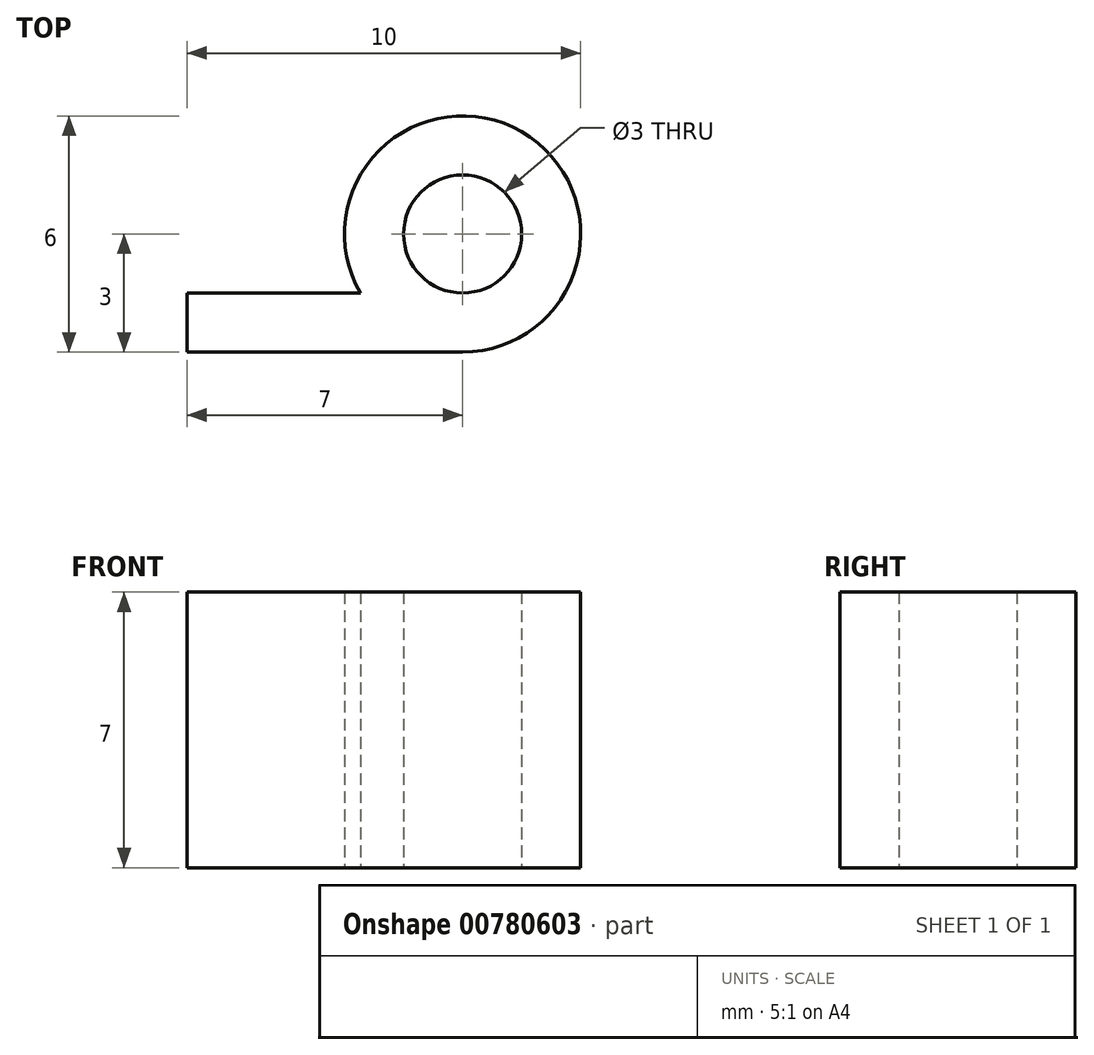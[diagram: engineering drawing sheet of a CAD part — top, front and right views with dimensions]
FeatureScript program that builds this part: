
annotation { "Feature Type Name" : "Feature", "Feature Type Description" : "" }
export const myFeature = defineFeature(function(context is Context, id is Id, definition is map)
    precondition{}
    {
        {
            var Q0;
            Q0=qCreatedBy(makeId("Top.planeOp"),FACE);
            var sketch = newSketch(context, id + "F0", { "sketchPlane" : qUnion([Q0])});
            skCircle(sketch, "E0", {"center": v(0, 0) * mm, "radius": 1.5 * mm});
            skLineSegment(sketch, "E1", {"start": v(0, 0) * mm, "end": v(0, -3) * mm});
            skLineSegment(sketch, "E2", {"start": v(0, -3) * mm, "end": v(-7, -3) * mm});
            skCircle(sketch, "E3", {"center": v(0, 0) * mm, "radius": 3 * mm});
            skLineSegment(sketch, "E4", {"start": v(0, -1.5) * mm, "end": v(-7, -1.5) * mm});
            skLineSegment(sketch, "E5", {"start": v(-7, -1.5) * mm, "end": v(-7, -3) * mm});
            skSolve(sketch);
        }
        {
            var Q0;
            {var subQ0=sQuery(id+"F0.wireOp",EDGE,"E2");Q0=makeQuery(id+"F0.imprint","IMPRINT",FACE,{"disambiguationData":[TD([[makeQuery(id+"F0.imprint","IMPRINT",EDGE,{"derivedFrom":subQ0}),-1.0]])]});}
            var Q1;
            {var subQ0=sQuery(id+"F0.wireOp",EDGE,"E0");Q1=makeQuery(id+"F0.imprint","IMPRINT",FACE,{"disambiguationData":[TD([[makeQuery(id+"F0.imprint","IMPRINT",EDGE,{"derivedFrom":subQ0}),-1.0]])]});}
            var Q2;
            {var subQ0=sQuery(id+"F0.wireOp",EDGE,"E3");var subQ3=sQuery(id+"F0.wireOp",EDGE,"E4");var subQ5=makeQuery(id+"F0.imprint","INTERSECT",VERTEX,{"derivedFrom":[subQ0,subQ3]});Q2=makeQuery(id+"F0.imprint","IMPRINT",FACE,{"disambiguationData":[TD([[makeQuery(id+"F0.imprint","IMPRINT",EDGE,{"disambiguationData":[TD([[subQ5,-1.0]])],"derivedFrom":subQ0}),1.0]])]});}
            extrude(context, id + "F1", {"entities" : qUnion([Q0, Q1, Q2]), "depth" : 7 * mm, "offsetDistance" : 25 * mm});
        }
    });
